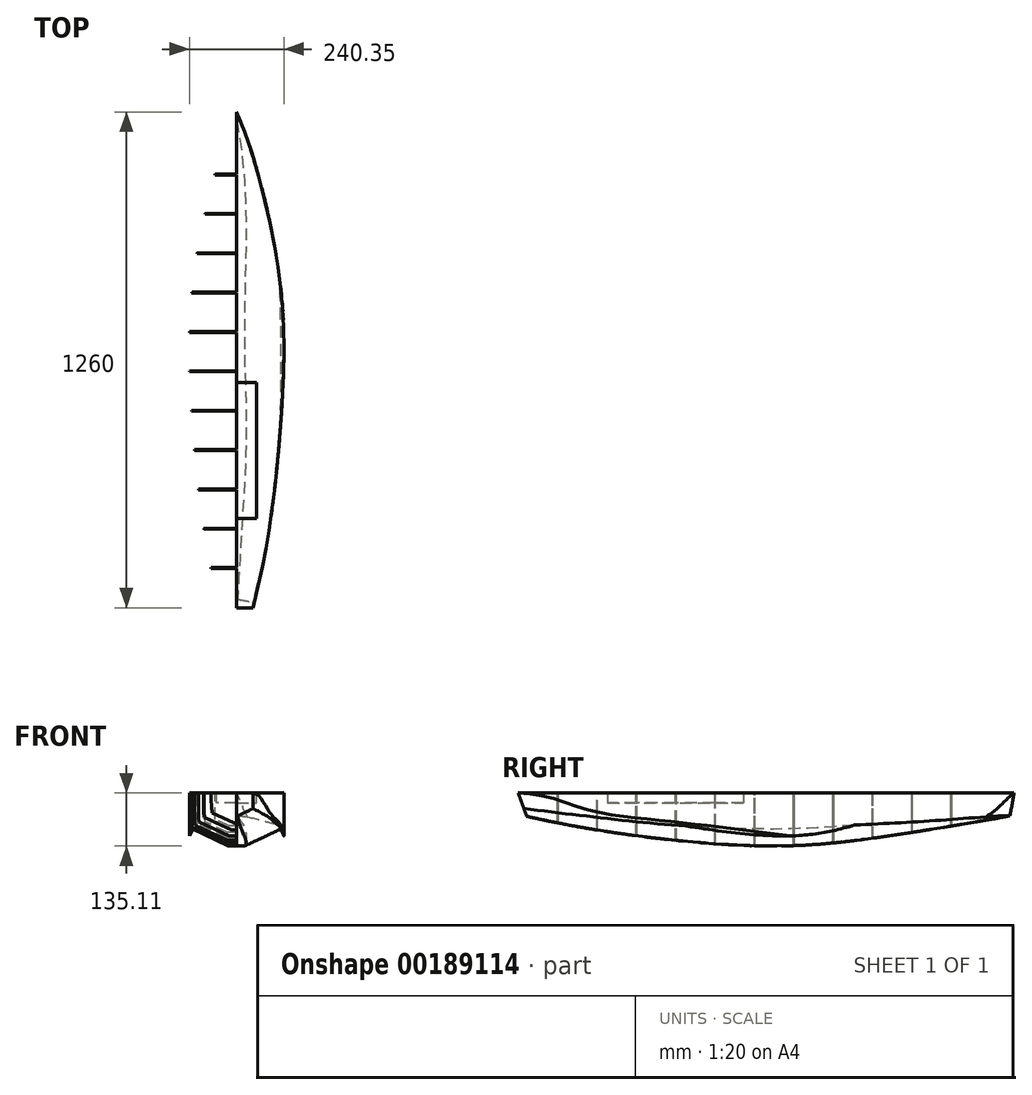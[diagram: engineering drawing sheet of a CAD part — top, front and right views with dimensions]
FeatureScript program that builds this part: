
annotation { "Feature Type Name" : "Feature", "Feature Type Description" : "" }
export const myFeature = defineFeature(function(context is Context, id is Id, definition is map)
    precondition{}
    {
        {
            var Q0;
            Q0=qCreatedBy(makeId("Top.planeOp"),FACE);
            var sketch = newSketch(context, id + "F0", { "sketchPlane" : qUnion([Q0])});
            skLineSegment(sketch, "E0", {"start": v(0, 1260) * mm, "end": v(0, 0) * mm});
            skLineSegment(sketch, "E1", {"start": v(0, 0) * mm, "end": v(41.48, 0) * mm});
            skFitSpline(sketch, "E2", {"points": [v(41.48, 0) * mm, v(90.65, 253.98) * mm, v(120, 627.11) * mm, v(97.7, 912.65) * mm, v(0, 1260) * mm], "startDerivative": vector(344.36, 1385.58) * mm, "endDerivative": vector(-474.1, 1079.88) * mm});
            skSolve(sketch);
        }
        {
            var Q0;
            Q0=sQuery(id+"F0.wireOp",EDGE,"E0");
            var Q1;
            Q1=qCreatedBy(makeId("Top.planeOp"),FACE);
            cPlane(context, id + "F1", {"entities" : qUnion([Q0, Q1]), "cplaneType" : CPlaneType.LINE_ANGLE, "offset" : 25 * mm, "angle" : 175 * degree, "width" : 150 * mm, "height" : 150 * mm});
        }
        {
            var Q0;
            Q0=sQuery(id+"F0.wireOp",VERTEX,"E2.2.internal");
            var Q1;
            Q1=qCreatedBy(id+"F1.planeOp",FACE);
            cPlane(context, id + "F2", {"entities" : qUnion([Q0, Q1]), "cplaneType" : CPlaneType.PLANE_POINT, "offset" : 25 * mm, "width" : 150 * mm, "height" : 150 * mm});
        }
        {
            var Q0;
            Q0=qCreatedBy(id+"F2.planeOp",FACE);
            var sketch = newSketch(context, id + "F3", { "sketchPlane" : qUnion([Q0])});
            skFitSpline(sketch, "E3.0", {"points": [v(41.32, 0) * mm, v(67.1, 104.12) * mm, v(93.08, 238.21) * mm, v(128.7, 637.96) * mm, v(108.4, 902.75) * mm, v(41.91, 1164.17) * mm, v(0, 1260) * mm]});
            skLineSegment(sketch, "E4", {"start": v(41.32, 0) * mm, "end": v(183.65, 0) * mm});
            skLineSegment(sketch, "E5", {"start": v(183.65, 0) * mm, "end": v(161.92, 1260) * mm});
            skLineSegment(sketch, "E6", {"start": v(161.92, 1260) * mm, "end": v(0, 1260) * mm});
            skSolve(sketch);
        }
        {
            var Q0;
            Q0=qCreatedBy(makeId("Front.planeOp"),FACE);
            var Q1;
            Q1=sQuery(id+"F0.wireOp",VERTEX,"E2.2.internal");
            cPlane(context, id + "F4", {"entities" : qUnion([Q0, Q1]), "cplaneType" : CPlaneType.PLANE_POINT, "offset" : 25 * mm, "width" : 150 * mm, "height" : 150 * mm});
        }
        {
            var Q0;
            Q0=qCreatedBy(id+"F4.planeOp",FACE);
            var sketch = newSketch(context, id + "F5", { "sketchPlane" : qUnion([Q0])});
            skLineSegment(sketch, "E7", {"start": v(120, 0) * mm, "end": v(111.94, -92.13) * mm});
            skLineSegment(sketch, "E8", {"start": v(111.94, -92.13) * mm, "end": v(20, -135) * mm});
            skLineSegment(sketch, "E9", {"start": v(20, -135) * mm, "end": v(0, -135) * mm});
            skPoint(sketch, "E10.0", {"position": v(120, 0) * mm});
            skLineSegment(sketch, "E11", {"start": v(0, 0) * mm, "end": v(120, 0) * mm});
            skLineSegment(sketch, "E12", {"start": v(0, -135) * mm, "end": v(0, 0) * mm});
            skSolve(sketch);
        }
        {
            var Q0;
            Q0=qCreatedBy(makeId("Right.planeOp"),FACE);
            var sketch = newSketch(context, id + "F6", { "sketchPlane" : qUnion([Q0])});
            skLineSegment(sketch, "E13", {"start": v(0, 0) * mm, "end": v(0, -54.68) * mm});
            skPoint(sketch, "E14.0", {"position": v(1260, 0) * mm});
            skLineSegment(sketch, "E15", {"start": v(1260, 0) * mm, "end": v(1260, -57.13) * mm});
            skPoint(sketch, "E16.0", {"position": v(627.11, -135) * mm});
            skFitSpline(sketch, "E17", {"points": [v(1260, -57.13) * mm, v(922.12, -112.2) * mm, v(627.11, -135) * mm, v(228.29, -98.73) * mm, v(0, -54.68) * mm], "startDerivative": vector(-1339.84, -234.26) * mm, "endDerivative": vector(-966.3, 222.1) * mm});
            skPoint(sketch, "E18.0", {"position": v(627.11, -92.13) * mm});
            skFitSpline(sketch, "E19", {"points": [v(0, -37.66) * mm, v(370.7, -82.93) * mm, v(627.11, -92.13) * mm, v(992.2, -77.79) * mm, v(1260, -57.13) * mm], "startDerivative": vector(1443.46, -196.28) * mm, "endDerivative": vector(1089.36, 93.68) * mm});
            skLineSegment(sketch, "E20", {"start": v(1260, -57.13) * mm, "end": v(1260, -197.91) * mm});
            skLineSegment(sketch, "E21", {"start": v(1260, -197.91) * mm, "end": v(0, -197.91) * mm});
            skLineSegment(sketch, "E22", {"start": v(0, -197.91) * mm, "end": v(0, -54.68) * mm});
            skSolve(sketch);
        }
        {
            var Q0;
            Q0=sQuery(id+"F5.wireOp",EDGE,"E8");
            cPlane(context, id + "F7", {"entities" : qUnion([Q0]), "cplaneType" : CPlaneType.LINE_ANGLE, "offset" : 25 * mm, "angle" : 90 * degree, "width" : 150 * mm, "height" : 150 * mm});
        }
        {
            var Q0;
            Q0=qCreatedBy(id+"F7.planeOp",FACE);
            var sketch = newSketch(context, id + "F8", { "sketchPlane" : qUnion([Q0])});
            skPoint(sketch, "E23.0", {"position": v(62.52, 627.11) * mm});
            skLineSegment(sketch, "E24", {"start": v(62.52, 627.11) * mm, "end": v(62.52, 686.27) * mm});
            skSolve(sketch);
        }
        {
            var Q0;
            Q0=sQuery(id+"F8.wireOp",EDGE,"E24");
            var Q1;
            Q1=qCreatedBy(id+"F7.planeOp",FACE);
            cPlane(context, id + "F9", {"entities" : qUnion([Q0, Q1]), "cplaneType" : CPlaneType.LINE_ANGLE, "offset" : 25 * mm, "angle" : 90 * degree, "width" : 150 * mm, "height" : 150 * mm});
        }
        {
            var Q0;
            Q0=qCreatedBy(id+"F9.planeOp",FACE);
            var sketch = newSketch(context, id + "F10", { "sketchPlane" : qUnion([Q0])});
            skFitSpline(sketch, "E25.0", {"points": [v(-1260, -49.66) * mm, v(-1247.63, -52.88) * mm, v(-1222.67, -59.03) * mm, v(-1184.78, -67.57) * mm, v(-1146.54, -75.55) * mm, v(-1108, -83) * mm, v(-1069.2, -89.97) * mm, v(-1036.68, -95.37) * mm, v(-1010.55, -99.46) * mm, v(-990.9, -102.4) * mm, v(-974.47, -104.76) * mm, v(-961.3, -106.59) * mm, v(-948.12, -108.38) * mm, v(-931.64, -110.53) * mm, v(-905.26, -113.82) * mm, v(-872.25, -117.6) * mm, v(-832.6, -121.56) * mm, v(-792.88, -124.84) * mm, v(-753.12, -127.42) * mm, v(-700.02, -129.9) * mm, v(-646.81, -130.96) * mm, v(-593.52, -130.72) * mm, v(-553.53, -129.85) * mm, v(-513.5, -128.24) * mm, v(-483.45, -126.44) * mm, v(-463.4, -124.98) * mm, v(-450.04, -123.94) * mm, v(-433.36, -122.52) * mm, v(-413.37, -120.62) * mm, v(-386.76, -117.85) * mm, v(-353.57, -113.95) * mm, v(-313.84, -108.7) * mm, v(-274.2, -102.96) * mm, v(-234.65, -96.78) * mm, v(-195.22, -90.15) * mm, v(-155.92, -83.01) * mm, v(-116.77, -75.37) * mm, v(-77.76, -67.3) * mm, v(-38.84, -58.9) * mm, v(-12.94, -53.16) * mm, v(0, -50.27) * mm]});
            skLineSegment(sketch, "E26", {"start": v(0, -50.27) * mm, "end": v(0, -201.87) * mm});
            skLineSegment(sketch, "E27", {"start": v(0, -201.87) * mm, "end": v(-1260, -201.87) * mm});
            skLineSegment(sketch, "E28", {"start": v(-1260, -201.87) * mm, "end": v(-1260, -49.66) * mm});
            skSolve(sketch);
        }
        {
            var Q0;
            Q0=makeQuery(id+"F0.imprint","IMPRINT",FACE,{"disambiguationData":[TD([[makeQuery(id+"F0.imprint","IMPRINT",EDGE,{"derivedFrom":sQuery(id+"F0.wireOp",EDGE,"E0")}),1.0]])]});
            extrude(context, id + "F11", {"entities" : qUnion([Q0]), "oppositeDirection" : true, "depth" : 153 * mm});
        }
        {
            var Q0;
            Q0=makeQuery(id+"F3.imprint","IMPRINT",FACE,{"disambiguationData":[TD([[makeQuery(id+"F3.imprint","IMPRINT",EDGE,{"derivedFrom":sQuery(id+"F3.wireOp",EDGE,"E3.0")}),-1.0]])]});
            extrude(context, id + "F12", {"entities" : qUnion([Q0]), "operationType" : NewBodyOperationType.REMOVE, "oppositeDirection" : true, "depth" : 121 * mm});
        }
        {
            var Q0;
            Q0=makeQuery(id+"F10.imprint","IMPRINT",FACE,{"disambiguationData":[TD([[makeQuery(id+"F10.imprint","IMPRINT",EDGE,{"derivedFrom":sQuery(id+"F10.wireOp",EDGE,"E25.0")}),-1.0]])]});
            extrude(context, id + "F13", {"entities" : qUnion([Q0]), "operationType" : NewBodyOperationType.REMOVE, "depth" : 154 * mm});
        }
        {
            var Q0;
            Q0=makeQuery(id+"F6.imprint","IMPRINT",FACE,{"disambiguationData":[TD([[makeQuery(id+"F6.imprint","IMPRINT",EDGE,{"derivedFrom":sQuery(id+"F6.wireOp",EDGE,"E17")}),1.0]])]});
            extrude(context, id + "F14", {"entities" : qUnion([Q0]), "operationType" : NewBodyOperationType.REMOVE, "depth" : 139 * mm});
        }
        {
            var Q0;
            Q0=makeQuery(id+"F11.opExtrude","SWEPT_BODY",BODY,{"disambiguationData":[OSD([sQuery(id+"F0.wireOp",EDGE,"E0"),sQuery(id+"F0.wireOp",EDGE,"E1"),sQuery(id+"F0.wireOp",EDGE,"E2")])]});
            var Q1;
            Q1=qCreatedBy(makeId("Right.planeOp"),FACE);
            mirror(context, id + "F15", {"operationType" : NewBodyOperationType.ADD, "entities" : qUnion([Q0]), "mirrorPlane" : qUnion([Q1])});
        }
        {
            var Q0;
            Q0=qCreatedBy(makeId("Top.planeOp"),FACE);
            var sketch = newSketch(context, id + "F16", { "sketchPlane" : qUnion([Q0])});
            skPoint(sketch, "E29.0", {"position": v(0, 1260) * mm});
            skLineSegment(sketch, "E30.bottom", {"start": v(0, 1260) * mm, "end": v(-131.37, 1260) * mm});
            skLineSegment(sketch, "E30.top", {"start": v(0, 0) * mm, "end": v(-131.37, 0) * mm});
            skLineSegment(sketch, "E30.left", {"start": v(0, 1260) * mm, "end": v(0, 0) * mm});
            skLineSegment(sketch, "E31.bottom", {"start": v(0, 100) * mm, "end": v(-131.37, 100) * mm});
            skLineSegment(sketch, "E31.top", {"start": v(0, 102) * mm, "end": v(-131.37, 102) * mm});
            skLineSegment(sketch, "E31.left", {"start": v(0, 100) * mm, "end": v(0, 102) * mm});
            skLineSegment(sketch, "E31.right", {"start": v(-131.37, 100) * mm, "end": v(-131.37, 102) * mm});
            skLineSegment(sketch, "E32.bottom", {"start": v(0, 300) * mm, "end": v(-131.37, 300) * mm});
            skLineSegment(sketch, "E32.top", {"start": v(0, 302) * mm, "end": v(-131.37, 302) * mm});
            skLineSegment(sketch, "E32.left", {"start": v(0, 300) * mm, "end": v(0, 302) * mm});
            skLineSegment(sketch, "E32.right", {"start": v(-131.37, 300) * mm, "end": v(-131.37, 302) * mm});
            skLineSegment(sketch, "E33.bottom", {"start": v(0, 400) * mm, "end": v(-131.37, 400) * mm});
            skLineSegment(sketch, "E33.top", {"start": v(0, 402) * mm, "end": v(-131.37, 402) * mm});
            skLineSegment(sketch, "E33.left", {"start": v(0, 400) * mm, "end": v(0, 402) * mm});
            skLineSegment(sketch, "E33.right", {"start": v(-131.37, 400) * mm, "end": v(-131.37, 402) * mm});
            skLineSegment(sketch, "E34.bottom", {"start": v(0, 500) * mm, "end": v(-131.37, 500) * mm});
            skLineSegment(sketch, "E34.top", {"start": v(0, 502) * mm, "end": v(-131.37, 502) * mm});
            skLineSegment(sketch, "E34.left", {"start": v(0, 500) * mm, "end": v(0, 502) * mm});
            skLineSegment(sketch, "E34.right", {"start": v(-131.37, 500) * mm, "end": v(-131.37, 502) * mm});
            skLineSegment(sketch, "E35.bottom", {"start": v(0, 600) * mm, "end": v(-131.37, 600) * mm});
            skLineSegment(sketch, "E35.top", {"start": v(0, 602) * mm, "end": v(-131.37, 602) * mm});
            skLineSegment(sketch, "E35.left", {"start": v(0, 600) * mm, "end": v(0, 602) * mm});
            skLineSegment(sketch, "E35.right", {"start": v(-131.37, 600) * mm, "end": v(-131.37, 602) * mm});
            skLineSegment(sketch, "E36.bottom", {"start": v(0, 200) * mm, "end": v(-131.37, 200) * mm});
            skLineSegment(sketch, "E36.top", {"start": v(0, 202) * mm, "end": v(-131.37, 202) * mm});
            skLineSegment(sketch, "E36.left", {"start": v(0, 200) * mm, "end": v(0, 202) * mm});
            skLineSegment(sketch, "E36.right", {"start": v(-131.37, 200) * mm, "end": v(-131.37, 202) * mm});
            skLineSegment(sketch, "E37.bottom", {"start": v(0, 702) * mm, "end": v(-131.37, 702) * mm});
            skLineSegment(sketch, "E37.top", {"start": v(0, 700) * mm, "end": v(-131.37, 700) * mm});
            skLineSegment(sketch, "E37.left", {"start": v(0, 700) * mm, "end": v(0, 702) * mm});
            skLineSegment(sketch, "E37.right", {"start": v(-131.37, 700) * mm, "end": v(-131.37, 702) * mm});
            skLineSegment(sketch, "E38.bottom", {"start": v(0, 800) * mm, "end": v(-131.37, 800) * mm});
            skLineSegment(sketch, "E38.top", {"start": v(0, 802) * mm, "end": v(-131.37, 802) * mm});
            skLineSegment(sketch, "E38.left", {"start": v(0, 800) * mm, "end": v(0, 802) * mm});
            skLineSegment(sketch, "E38.right", {"start": v(-131.37, 800) * mm, "end": v(-131.37, 802) * mm});
            skLineSegment(sketch, "E39.bottom", {"start": v(0, 900) * mm, "end": v(-131.37, 900) * mm});
            skLineSegment(sketch, "E39.top", {"start": v(0, 902) * mm, "end": v(-131.37, 902) * mm});
            skLineSegment(sketch, "E39.left", {"start": v(0, 900) * mm, "end": v(0, 902) * mm});
            skLineSegment(sketch, "E39.right", {"start": v(-131.37, 900) * mm, "end": v(-131.37, 902) * mm});
            skLineSegment(sketch, "E40.bottom", {"start": v(0, 1002) * mm, "end": v(-131.37, 1002) * mm});
            skLineSegment(sketch, "E40.top", {"start": v(0, 1000) * mm, "end": v(-131.37, 1000) * mm});
            skLineSegment(sketch, "E40.left", {"start": v(0, 1002) * mm, "end": v(0, 1000) * mm});
            skLineSegment(sketch, "E40.right", {"start": v(-131.37, 1002) * mm, "end": v(-131.37, 1000) * mm});
            skLineSegment(sketch, "E41.bottom", {"start": v(0, 1100) * mm, "end": v(-131.37, 1100) * mm});
            skLineSegment(sketch, "E41.top", {"start": v(0, 1102) * mm, "end": v(-131.37, 1102) * mm});
            skLineSegment(sketch, "E41.left", {"start": v(0, 1100) * mm, "end": v(0, 1102) * mm});
            skLineSegment(sketch, "E41.right", {"start": v(-131.37, 1100) * mm, "end": v(-131.37, 1102) * mm});
            skLineSegment(sketch, "E42", {"start": v(-131.37, 0) * mm, "end": v(-131.37, 1260) * mm});
            skSolve(sketch);
        }
        {
            var Q0;
            Q0=qCreatedBy(makeId("Top.planeOp"),FACE);
            var sketch = newSketch(context, id + "F17", { "sketchPlane" : qUnion([Q0])});
            skLineSegment(sketch, "E43.bottom", {"start": v(0, 227.25) * mm, "end": v(-50.65, 227.25) * mm});
            skLineSegment(sketch, "E43.top", {"start": v(0, 572.26) * mm, "end": v(-50.65, 572.26) * mm});
            skLineSegment(sketch, "E43.left", {"start": v(0, 227.25) * mm, "end": v(0, 572.26) * mm});
            skLineSegment(sketch, "E43.right", {"start": v(-50.65, 227.25) * mm, "end": v(-50.65, 572.26) * mm});
            skLineSegment(sketch, "E44.MirrorCS", {"start": v(0, 227.25) * mm, "end": v(50.65, 227.25) * mm});
            skLineSegment(sketch, "E45.MirrorCS", {"start": v(50.65, 227.25) * mm, "end": v(50.65, 572.26) * mm});
            skLineSegment(sketch, "E46.MirrorCS", {"start": v(0, 572.26) * mm, "end": v(50.65, 572.26) * mm});
            skSolve(sketch);
        }
        {
            var Q0;
            Q0=makeQuery(id+"F17.imprint","IMPRINT",FACE,{"disambiguationData":[TD([[makeQuery(id+"F17.imprint","IMPRINT",EDGE,{"derivedFrom":sQuery(id+"F17.wireOp",EDGE,"E43.left")}),-1.0]])]});
            var Q1;
            Q1=makeQuery(id+"F17.imprint","IMPRINT",FACE,{"disambiguationData":[TD([[makeQuery(id+"F17.imprint","IMPRINT",EDGE,{"derivedFrom":sQuery(id+"F17.wireOp",EDGE,"E43.bottom")}),-1.0]])]});
            extrude(context, id + "F18", {"entities" : qUnion([Q0, Q1]), "operationType" : NewBodyOperationType.REMOVE, "oppositeDirection" : true, "depth" : 25 * mm});
        }
        {
            var Q0;
            {var subQ0=makeQuery(id+"F11.opExtrude","CAP_EDGE",EDGE,{"disambiguationData":[OSD([sQuery(id+"F0.wireOp",EDGE,"E1")])],"isStart":true});Q0=makeQuery(id+"F15.boolean.opBoolean","MERGE",EDGE,{"derivedFrom":[subQ0,makeQuery(id+"F15.opPattern","COPY",EDGE,{"derivedFrom":subQ0,"instanceName":"1"})]});}
            var Q1;
            Q1=qCreatedBy(makeId("Top.planeOp"),FACE);
            cPlane(context, id + "F19", {"entities" : qUnion([Q0, Q1]), "cplaneType" : CPlaneType.LINE_ANGLE, "offset" : 25 * mm, "angle" : 20 * degree, "width" : 150 * mm, "height" : 150 * mm});
        }
        {
            var Q0;
            Q0=qCreatedBy(id+"F19.planeOp",FACE);
            var sketch = newSketch(context, id + "F20", { "sketchPlane" : qUnion([Q0])});
            skLineSegment(sketch, "E47.bottom", {"start": v(0, 0) * mm, "end": v(-52.06, 0) * mm});
            skLineSegment(sketch, "E47.top", {"start": v(0, 28.9) * mm, "end": v(-52.06, 28.9) * mm});
            skLineSegment(sketch, "E47.left", {"start": v(0, 0) * mm, "end": v(0, 28.9) * mm});
            skLineSegment(sketch, "E47.right", {"start": v(-52.06, 0) * mm, "end": v(-52.06, 28.9) * mm});
            skLineSegment(sketch, "E48.MirrorCS", {"start": v(0, 28.9) * mm, "end": v(52.06, 28.9) * mm});
            skLineSegment(sketch, "E49.MirrorCS", {"start": v(52.06, 0) * mm, "end": v(52.06, 28.9) * mm});
            skLineSegment(sketch, "E50.MirrorCS", {"start": v(0, 0) * mm, "end": v(52.06, 0) * mm});
            skSolve(sketch);
        }
        {
            var Q0;
            Q0=makeQuery(id+"F20.imprint","IMPRINT",FACE,{"disambiguationData":[TD([[makeQuery(id+"F20.imprint","IMPRINT",EDGE,{"derivedFrom":sQuery(id+"F20.wireOp",EDGE,"E47.left")}),-1.0]])]});
            var Q1;
            Q1=makeQuery(id+"F20.imprint","IMPRINT",FACE,{"disambiguationData":[TD([[makeQuery(id+"F20.imprint","IMPRINT",EDGE,{"derivedFrom":sQuery(id+"F20.wireOp",EDGE,"E47.bottom")}),-1.0]])]});
            extrude(context, id + "F21", {"entities" : qUnion([Q0, Q1]), "operationType" : NewBodyOperationType.REMOVE, "depth" : 79 * mm});
        }
        {
            var Q0;
            {var subQ0=sQuery(id+"F16.wireOp",EDGE,"E30.top");Q0=makeQuery(id+"F16.imprint","IMPRINT",FACE,{"disambiguationData":[TD([[makeQuery(id+"F16.imprint","IMPRINT",EDGE,{"derivedFrom":subQ0}),-1.0]])]});}
            var Q1;
            {var subQ0=sQuery(id+"F16.wireOp",EDGE,"E32.bottom");Q1=makeQuery(id+"F16.imprint","IMPRINT",FACE,{"disambiguationData":[TD([[makeQuery(id+"F16.imprint","IMPRINT",EDGE,{"derivedFrom":subQ0}),1.0]])]});}
            var Q2;
            {var subQ0=sQuery(id+"F16.wireOp",EDGE,"E32.top");Q2=makeQuery(id+"F16.imprint","IMPRINT",FACE,{"disambiguationData":[TD([[makeQuery(id+"F16.imprint","IMPRINT",EDGE,{"derivedFrom":subQ0}),-1.0]])]});}
            var Q3;
            {var subQ0=sQuery(id+"F16.wireOp",EDGE,"E33.top");Q3=makeQuery(id+"F16.imprint","IMPRINT",FACE,{"disambiguationData":[TD([[makeQuery(id+"F16.imprint","IMPRINT",EDGE,{"derivedFrom":subQ0}),-1.0]])]});}
            var Q4;
            {var subQ0=sQuery(id+"F16.wireOp",EDGE,"E31.top");Q4=makeQuery(id+"F16.imprint","IMPRINT",FACE,{"disambiguationData":[TD([[makeQuery(id+"F16.imprint","IMPRINT",EDGE,{"derivedFrom":subQ0}),-1.0]])]});}
            var Q5;
            {var subQ0=sQuery(id+"F16.wireOp",EDGE,"E34.top");Q5=makeQuery(id+"F16.imprint","IMPRINT",FACE,{"disambiguationData":[TD([[makeQuery(id+"F16.imprint","IMPRINT",EDGE,{"derivedFrom":subQ0}),-1.0]])]});}
            var Q6;
            {var subQ0=sQuery(id+"F16.wireOp",EDGE,"E35.top");Q6=makeQuery(id+"F16.imprint","IMPRINT",FACE,{"disambiguationData":[TD([[makeQuery(id+"F16.imprint","IMPRINT",EDGE,{"derivedFrom":subQ0}),-1.0]])]});}
            var Q7;
            {var subQ0=sQuery(id+"F16.wireOp",EDGE,"E37.bottom");Q7=makeQuery(id+"F16.imprint","IMPRINT",FACE,{"disambiguationData":[TD([[makeQuery(id+"F16.imprint","IMPRINT",EDGE,{"derivedFrom":subQ0}),-1.0]])]});}
            var Q8;
            {var subQ0=sQuery(id+"F16.wireOp",EDGE,"E38.top");Q8=makeQuery(id+"F16.imprint","IMPRINT",FACE,{"disambiguationData":[TD([[makeQuery(id+"F16.imprint","IMPRINT",EDGE,{"derivedFrom":subQ0}),-1.0]])]});}
            var Q9;
            {var subQ0=sQuery(id+"F16.wireOp",EDGE,"E39.top");Q9=makeQuery(id+"F16.imprint","IMPRINT",FACE,{"disambiguationData":[TD([[makeQuery(id+"F16.imprint","IMPRINT",EDGE,{"derivedFrom":subQ0}),-1.0]])]});}
            var Q10;
            {var subQ0=sQuery(id+"F16.wireOp",EDGE,"E40.bottom");Q10=makeQuery(id+"F16.imprint","IMPRINT",FACE,{"disambiguationData":[TD([[makeQuery(id+"F16.imprint","IMPRINT",EDGE,{"derivedFrom":subQ0}),-1.0]])]});}
            var Q11;
            {var subQ0=sQuery(id+"F16.wireOp",EDGE,"E30.bottom");Q11=makeQuery(id+"F16.imprint","IMPRINT",FACE,{"disambiguationData":[TD([[makeQuery(id+"F16.imprint","IMPRINT",EDGE,{"derivedFrom":subQ0}),1.0]])]});}
            extrude(context, id + "F22", {"entities" : qUnion([Q0, Q1, Q2, Q3, Q4, Q5, Q6, Q7, Q8, Q9, Q10, Q11]), "operationType" : NewBodyOperationType.REMOVE, "oppositeDirection" : true, "depth" : 140 * mm});
        }
    });
